# Revit family: RN 90091 Optifitt-Serra-Verschlusszapfen
name_source: partatom
category: Rohrformteile
units: mm (PartAtom-declared; Revit-internal decimal feet)

## family parameters
Arbeitsebenenbasiert = Nein
Beim Laden mit Abzugskörper schneiden = Nein
Bemaßung runder Anschluss = Durchmesser verwenden
Gemeinsam genutzt = Nein
Immer vertikal = Ja
Teiletyp = Nicht definiert

## types (8) — shared parameters
1.010.00.2 Blattnummer der Richtlinie = 29
1.010.00.3 Ausgabedatum (Monat) der Richtlinie = 201308
1.010.00.4 Herstellername = R. Nussbaum AG
1.010.00.5 Revisionsdatum der Datei = 20190521
1.010.00.6 Webadresse des Herstellers = http://www.nussbaum.ch
1.100.00.4 Produktbezeichnung = Versorgung
1.110.00.2 Index = 3
1.110.00.4 Produktbezeichnung = Optifitt-Serra
1.960/3L.00.8 Link (URL) = https://www.nussbaum.ch
29.700.00.4 Produktname = Optifitt-Serra-Verschlusszapfen
29.700.00.5 Produktkennung = 2
29.700.00.6 Querschnittsform = 1
29.700.00.7 Nennweitensystem = DN
29.700.00.8 Nenndrucksystem = PN
29.710.02.4 Nenndruck = 16
29.710.02.5 max. zul. Überdruck [hPa] = 1600
29.710.02.7 max. zul. Dauer-Betriebsdruck [hPa] = 1600
29.710.02.9 max. zul. Dauer-Betriebstemperatur [°C] = 90
Connector Visibility = Nein
EnclosingSpace Visibility = Nein
Hersteller = R. Nussbaum AG
URL = https://www.nussbaum.ch

## per-type parameters (varying)
| type | 1.800.00.3 TGA-Nummer | 1.800.00.4 Kommentarfeld | 1.810.00.3 Hersteller-Bestellnummer | 1.810.00.4 DATANORM-Nummer | 1.810.00.5 StLB-Nummer | 1.810.00.6 GTIN-Nummer | 29.710.02.10 Formstück-Gewicht [kg] | 29.710.02.3 Benennung | CONNECTOR0_DIAMETER_dX_0r | CONNECTOR0_dX_01 | CONNECTOR0_ref_dX | Modell | R. Nussbaum AG 90091.04 de Visibility | R. Nussbaum AG 90091.05 de Visibility | R. Nussbaum AG 90091.06 de Visibility | R. Nussbaum AG 90091.07 de Visibility | R. Nussbaum AG 90091.08 de Visibility | R. Nussbaum AG 90091.09 de Visibility | R. Nussbaum AG 90091.10 de Visibility | R. Nussbaum AG 90091.11 de Visibility | Typenkommentare |
| DN=65 | 01900300000000000000000000000000000000000000000022000000000000000028 | 90091.10, Optifitt-Serra-Verschlusszapfen, DN=65, L=48, R=2½ | 90091.1 | 90091.1 | 216.118 | 7612945680716 | 0.663 | Optifitt-Serra-Verschlusszapfen, DN=65, L=48, R=2½ | 65 mm | 27 mm | 27 mm | 90091.1 | Nein | Nein | Nein | Nein | Nein | Nein | Ja | Nein | Optifitt-Serra-Verschlusszapfen  DN=65 |
| DN=80 | 01900300000000000000000000000000000000000000000022000000000000000015 | 90091.11, Optifitt-Serra-Verschlusszapfen, DN=80, L=52, R=3 | 90091.11 | 90091.11 |  | 7612945680723 | 0.921 | Optifitt-Serra-Verschlusszapfen, DN=80, L=52, R=3 | 80 mm | 30 mm | 30 mm | 90091.11 | Nein | Nein | Nein | Nein | Nein | Nein | Nein | Ja | Optifitt-Serra-Verschlusszapfen  DN=80 |
| DN=50 | 01900300000000000000000000000000000000000000000022000000000000000014 | 90091.09, Optifitt-Serra-Verschlusszapfen, DN=50, L=38, R=2 | 90091.09 | 90091.09 | 216.117 | 7612945680709 | 0.271 | Optifitt-Serra-Verschlusszapfen, DN=50, L=38, R=2 | 50 mm | 19 mm | 19 mm | 90091.09 | Nein | Nein | Nein | Nein | Nein | Ja | Nein | Nein | Optifitt-Serra-Verschlusszapfen  DN=50 |
| DN=40 | 01900300000000000000000000000000000000000000000022000000000000000013 | 90091.08, Optifitt-Serra-Verschlusszapfen, DN=40, L=37, R=1½ | 90091.08 | 90091.08 | 216.116 | 7612945680693 | 0.155 | Optifitt-Serra-Verschlusszapfen, DN=40, L=37, R=1½ | 40 mm | 19 mm | 19 mm | 90091.08 | Nein | Nein | Nein | Nein | Ja | Nein | Nein | Nein | Optifitt-Serra-Verschlusszapfen  DN=40 |
| DN=32 | 01900300000000000000000000000000000000000000000022000000000000000012 | 90091.07, Optifitt-Serra-Verschlusszapfen, DN=32, L=35, R=1¼ | 90091.07 | 90091.07 | 216.115 | 7612945680686 | 0.143 | Optifitt-Serra-Verschlusszapfen, DN=32, L=35, R=1¼ | 32 mm | 19 mm | 19 mm | 90091.07 | Nein | Nein | Nein | Ja | Nein | Nein | Nein | Nein | Optifitt-Serra-Verschlusszapfen  DN=32 |
| DN=25 | 01900300000000000000000000000000000000000000000022000000000000000011 | 90091.06, Optifitt-Serra-Verschlusszapfen, DN=25, L=32, R=1 | 90091.06 | 90091.06 | 216.114 | 7612945680679 | 0.001 | Optifitt-Serra-Verschlusszapfen, DN=25, L=32, R=1 | 25 mm  [stored 0.082021 ft] | 17 mm | 17 mm | 90091.06 | Nein | Nein | Ja | Nein | Nein | Nein | Nein | Nein | Optifitt-Serra-Verschlusszapfen  DN=25 |
| DN=20 | 01900300000000000000000000000000000000000000000022000000000000000010 | 90091.05, Optifitt-Serra-Verschlusszapfen, DN=20, L=27, R=¾ | 90091.05 | 90091.05 | 216.113 | 7612945680662 | 0.045 | Optifitt-Serra-Verschlusszapfen, DN=20, L=27, R=¾ | 20 mm | 15 mm | 15 mm | 90091.05 | Nein | Ja | Nein | Nein | Nein | Nein | Nein | Nein | Optifitt-Serra-Verschlusszapfen  DN=20 |
| DN=15 | 01900300000000000000000000000000000000000000000022000000000000000009 | 90091.04, Optifitt-Serra-Verschlusszapfen, DN=15, L=25, R=½ | 90091.04 | 90091.04 | 216.112 | 7612945680655 | 0.035 | Optifitt-Serra-Verschlusszapfen, DN=15, L=25, R=½ | 15 mm | 13 mm | 13 mm | 90091.04 | Ja | Nein | Nein | Nein | Nein | Nein | Nein | Nein | Optifitt-Serra-Verschlusszapfen  DN=15 |

note: [stored X ft] marks values corroborated as IEEE doubles in the binary element streams (Revit-internal decimal feet)

## geometry (parser evidence)
native form markers: Sweep x2
no freeform markers — native parametric forms only
